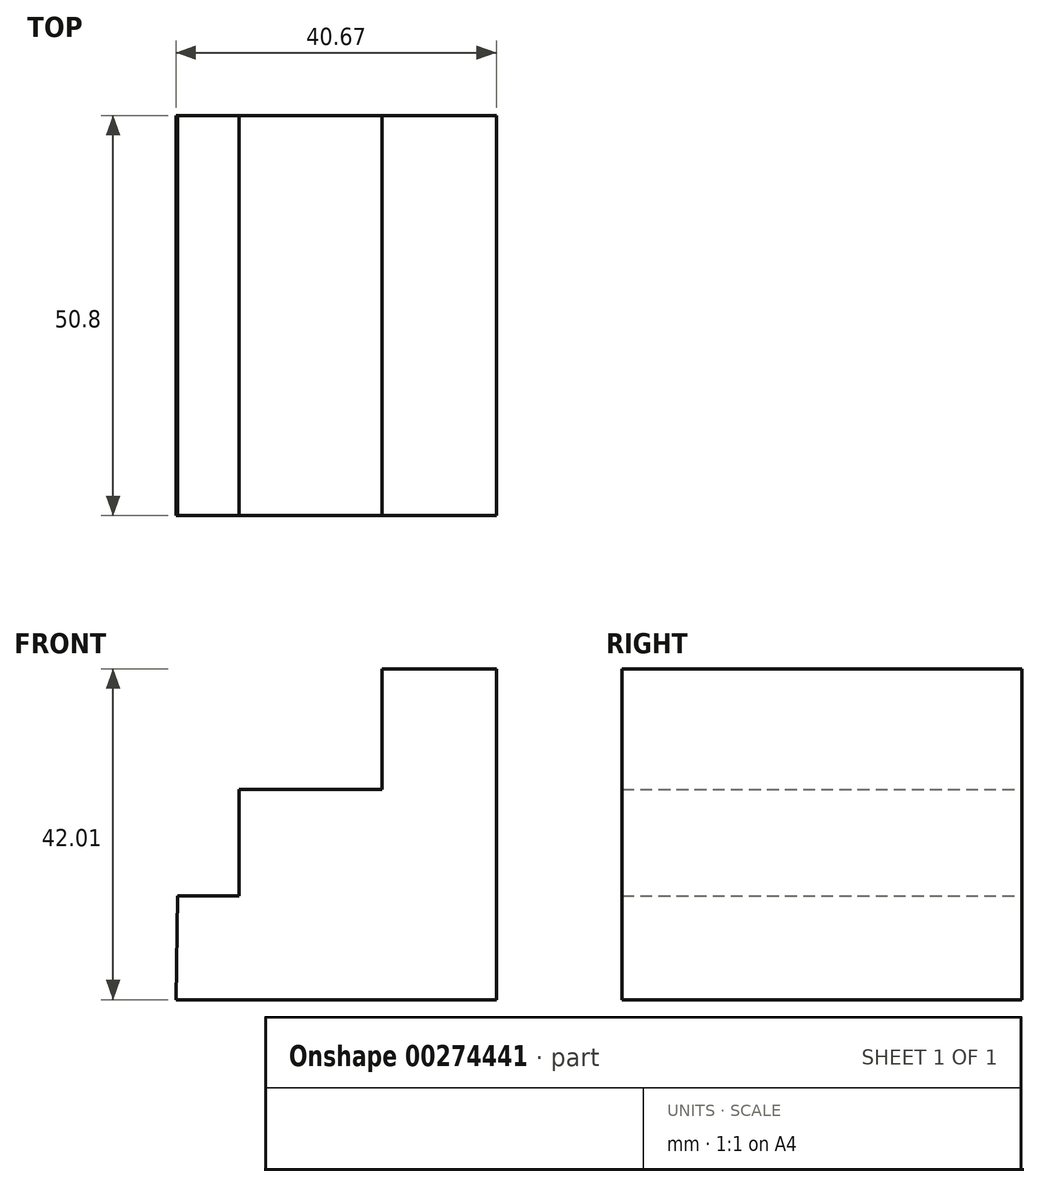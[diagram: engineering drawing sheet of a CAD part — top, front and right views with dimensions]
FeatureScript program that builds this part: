
annotation { "Feature Type Name" : "Feature", "Feature Type Description" : "" }
export const myFeature = defineFeature(function(context is Context, id is Id, definition is map)
    precondition{}
    {
        {
            var Q0;
            Q0=qCreatedBy(makeId("Front.planeOp"),FACE);
            var sketch = newSketch(context, id + "F0", { "sketchPlane" : qUnion([Q0])});
            skLineSegment(sketch, "E0", {"start": v(0, 0) * mm, "end": v(0, 42.01) * mm});
            skLineSegment(sketch, "E1", {"start": v(0, 0) * mm, "end": v(-40.67, 0) * mm});
            skLineSegment(sketch, "E2", {"start": v(0, 42.01) * mm, "end": v(-14.51, 42.01) * mm});
            skLineSegment(sketch, "E3", {"start": v(-14.51, 42.01) * mm, "end": v(-14.51, 26.73) * mm});
            skLineSegment(sketch, "E4", {"start": v(-14.51, 26.73) * mm, "end": v(-32.65, 26.73) * mm});
            skLineSegment(sketch, "E5", {"start": v(-32.65, 26.73) * mm, "end": v(-32.65, 13.18) * mm});
            skLineSegment(sketch, "E6", {"start": v(-32.65, 13.18) * mm, "end": v(-40.48, 13.18) * mm});
            skLineSegment(sketch, "E7", {"start": v(-40.48, 13.18) * mm, "end": v(-40.67, 0) * mm});
            skSolve(sketch);
        }
        {
            var Q0;
            Q0 = qSketchRegion(id + "F0", true);
            extrude(context, id + "F1", {"entities" : qUnion([Q0]), "depth" : 50.8 * mm});
        }
    });
